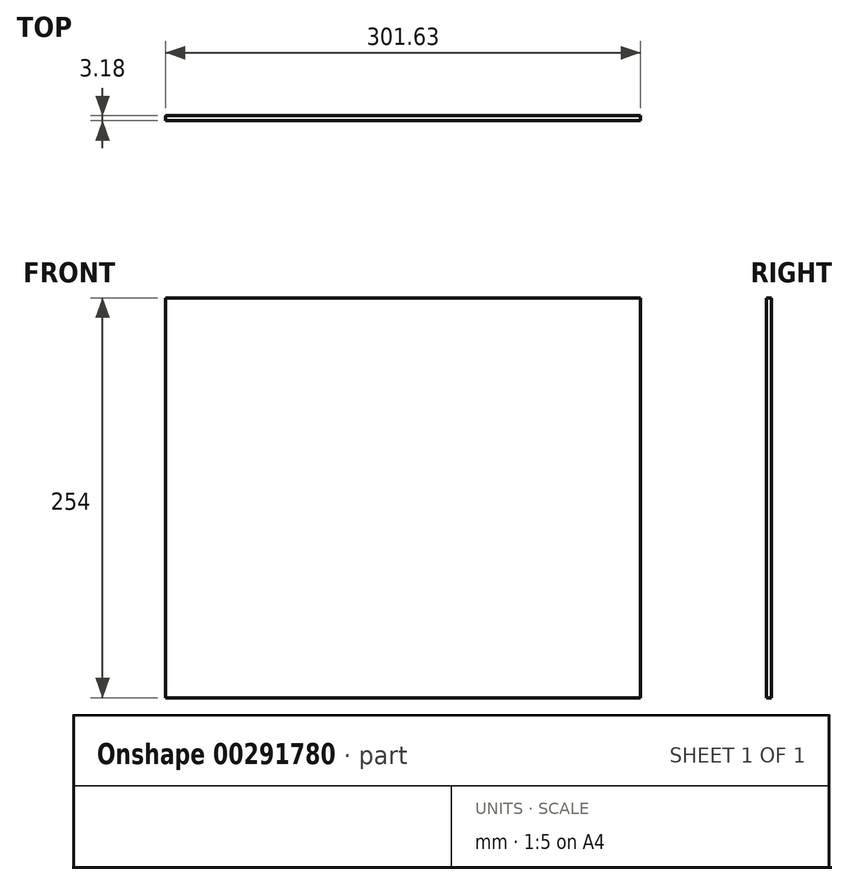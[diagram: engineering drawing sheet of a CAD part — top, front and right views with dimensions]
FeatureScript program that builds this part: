
annotation { "Feature Type Name" : "Feature", "Feature Type Description" : "" }
export const myFeature = defineFeature(function(context is Context, id is Id, definition is map)
    precondition{}
    {
        {
            var Q0;
            Q0=qCreatedBy(makeId("Front.planeOp"),FACE);
            var sketch = newSketch(context, id + "F0", { "sketchPlane" : qUnion([Q0])});
            skLineSegment(sketch, "E0.bottom", {"start": v(-457.2, -215.56) * mm, "end": v(-155.57, -215.56) * mm});
            skLineSegment(sketch, "E0.top", {"start": v(-457.2, -469.56) * mm, "end": v(-155.57, -469.56) * mm});
            skLineSegment(sketch, "E0.left", {"start": v(-457.2, -215.56) * mm, "end": v(-457.2, -469.56) * mm});
            skLineSegment(sketch, "E0.right", {"start": v(-155.57, -215.56) * mm, "end": v(-155.57, -469.56) * mm});
            skSolve(sketch);
        }
        {
            var Q0;
            Q0=makeQuery(id+"F0.imprint","IMPRINT",FACE,{"disambiguationData":[TD([[makeQuery(id+"F0.imprint","IMPRINT",EDGE,{"derivedFrom":sQuery(id+"F0.wireOp",EDGE,"E0.bottom")}),-1.0]])]});
            extrude(context, id + "F1", {"entities" : qUnion([Q0]), "endBound" : BoundingType.SYMMETRIC, "depth" : 3.17 * mm});
        }
    });
